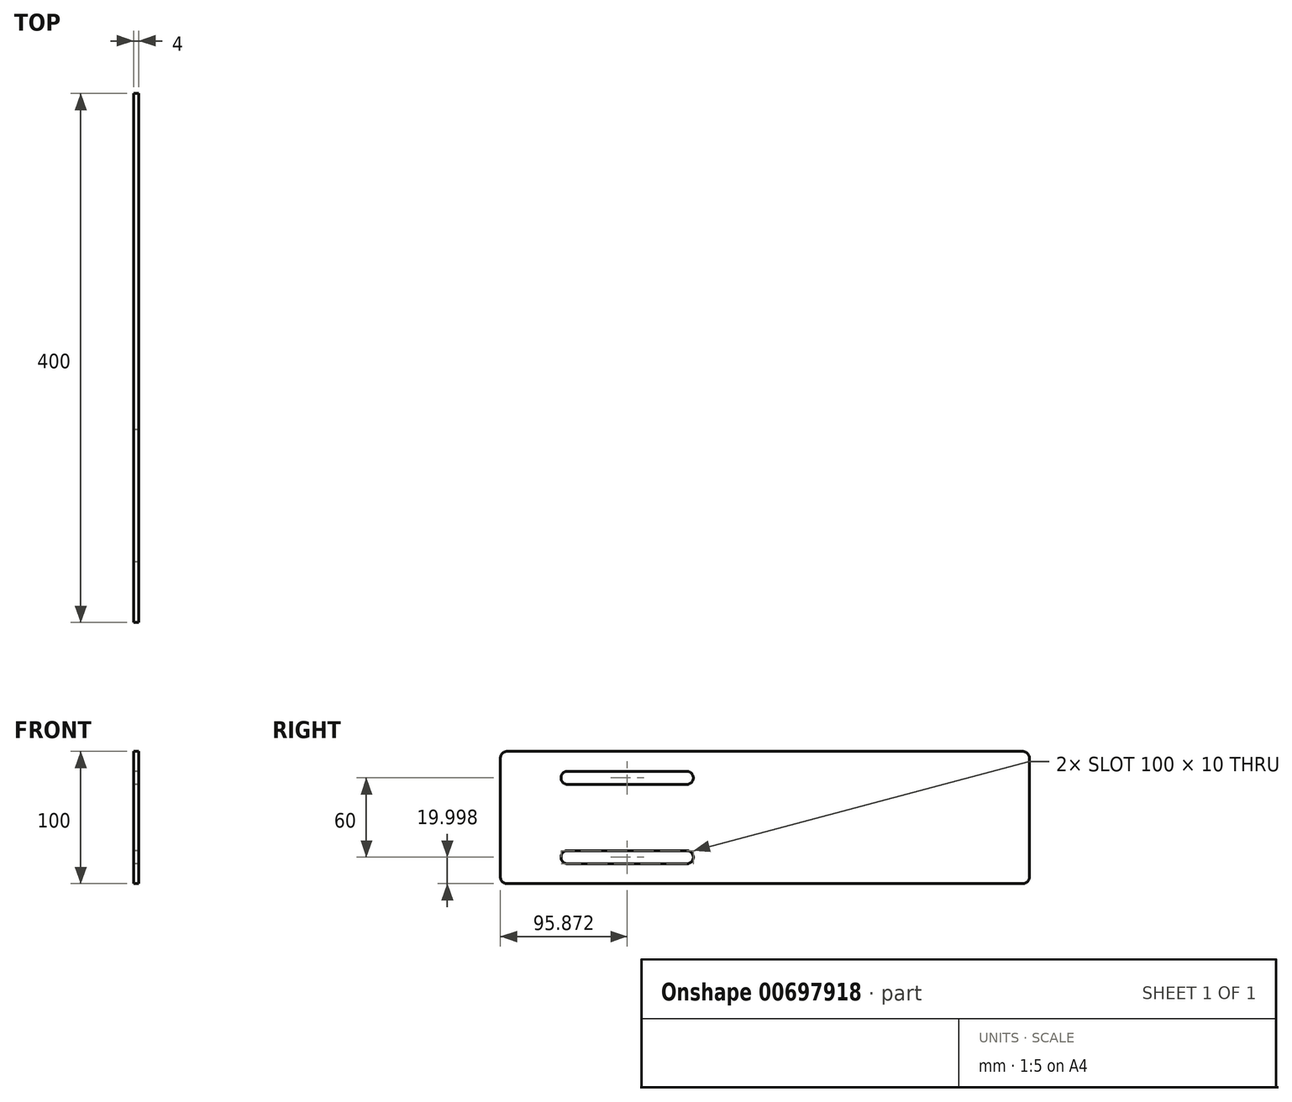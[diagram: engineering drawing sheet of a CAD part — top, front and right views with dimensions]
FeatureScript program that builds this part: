
annotation { "Feature Type Name" : "Feature", "Feature Type Description" : "" }
export const myFeature = defineFeature(function(context is Context, id is Id, definition is map)
    precondition{}
    {
        {
            var Q0;
            Q0=qCreatedBy(makeId("Right.planeOp"),FACE);
            var sketch = newSketch(context, id + "F0", { "sketchPlane" : qUnion([Q0])});
            skLineSegment(sketch, "E0.bottom", {"start": v(-184.31, 31.74) * mm, "end": v(205.69, 31.74) * mm});
            skLineSegment(sketch, "E0.top", {"start": v(-184.31, -68.26) * mm, "end": v(205.69, -68.26) * mm});
            skLineSegment(sketch, "E0.left", {"start": v(-189.31, 26.74) * mm, "end": v(-189.31, -63.26) * mm});
            skLineSegment(sketch, "E0.right", {"start": v(210.69, 26.74) * mm, "end": v(210.69, -63.26) * mm});
            skPoint(sketch, "E1.visualSharp", {"position": v(210.69, 31.74) * mm});
            skArc(sketch, "E1.filletArc", {"start": v(210.69, 26.74) * mm, "mid": v(209.22, 30.27) * mm, "end": v(205.69, 31.74) * mm});
            skPoint(sketch, "E2.visualSharp", {"position": v(210.69, -68.26) * mm});
            skArc(sketch, "E2.filletArc", {"start": v(205.69, -68.26) * mm, "mid": v(209.22, -66.8) * mm, "end": v(210.69, -63.26) * mm});
            skPoint(sketch, "E3.visualSharp", {"position": v(-189.31, -68.26) * mm});
            skArc(sketch, "E3.filletArc", {"start": v(-189.31, -63.26) * mm, "mid": v(-187.85, -66.8) * mm, "end": v(-184.31, -68.26) * mm});
            skPoint(sketch, "E4.visualSharp", {"position": v(-189.31, 31.74) * mm});
            skArc(sketch, "E4.filletArc", {"start": v(-184.31, 31.74) * mm, "mid": v(-187.85, 30.27) * mm, "end": v(-189.31, 26.74) * mm});
            skSolve(sketch);
        }
        {
            var Q0;
            Q0 = qSketchRegion(id + "F0", true);
            extrude(context, id + "F1", {"entities" : qUnion([Q0]), "depth" : 4 * mm, "offsetDistance" : 25 * mm});
        }
        {
            var Q0;
            Q0=qCreatedBy(makeId("Right.planeOp"),FACE);
            var sketch = newSketch(context, id + "F2", { "sketchPlane" : qUnion([Q0])});
            skLineSegment(sketch, "E5.bottom", {"start": v(-138.44, 16.74) * mm, "end": v(-48.44, 16.74) * mm});
            skLineSegment(sketch, "E5.top", {"start": v(-138.44, 6.74) * mm, "end": v(-48.44, 6.74) * mm});
            skLineSegment(sketch, "E5.left", {"start": v(-143.44, 11.74) * mm, "end": v(-143.44, 11.74) * mm});
            skLineSegment(sketch, "E5.right", {"start": v(-43.44, 11.74) * mm, "end": v(-43.44, 11.74) * mm});
            skPoint(sketch, "E6.firstSnap0", {"position": v(-143.44, 11.74) * mm});
            skLineSegment(sketch, "E6.bottom", {"start": v(-138.44, -43.26) * mm, "end": v(-48.44, -43.26) * mm});
            skLineSegment(sketch, "E6.top", {"start": v(-138.44, -53.26) * mm, "end": v(-48.44, -53.26) * mm});
            skLineSegment(sketch, "E6.left", {"start": v(-143.44, -48.26) * mm, "end": v(-143.44, -48.26) * mm});
            skLineSegment(sketch, "E6.right", {"start": v(-43.44, -48.26) * mm, "end": v(-43.44, -48.26) * mm});
            skPoint(sketch, "E7.visualSharp", {"position": v(-143.44, 16.74) * mm});
            skArc(sketch, "E7.filletArc", {"start": v(-138.44, 16.74) * mm, "mid": v(-141.97, 15.27) * mm, "end": v(-143.44, 11.74) * mm});
            skPoint(sketch, "E8.visualSharp", {"position": v(-143.44, 6.74) * mm});
            skArc(sketch, "E8.filletArc", {"start": v(-143.44, 11.74) * mm, "mid": v(-141.97, 8.2) * mm, "end": v(-138.44, 6.74) * mm});
            skPoint(sketch, "E9.visualSharp", {"position": v(-43.44, 6.74) * mm});
            skArc(sketch, "E9.filletArc", {"start": v(-48.44, 6.74) * mm, "mid": v(-44.9, 8.2) * mm, "end": v(-43.44, 11.74) * mm});
            skPoint(sketch, "E10.visualSharp", {"position": v(-43.44, 16.74) * mm});
            skArc(sketch, "E10.filletArc", {"start": v(-43.44, 11.74) * mm, "mid": v(-44.9, 15.27) * mm, "end": v(-48.44, 16.74) * mm});
            skPoint(sketch, "E11.visualSharp", {"position": v(-43.44, -43.26) * mm});
            skArc(sketch, "E11.filletArc", {"start": v(-43.44, -48.26) * mm, "mid": v(-44.9, -44.73) * mm, "end": v(-48.44, -43.26) * mm});
            skPoint(sketch, "E12.visualSharp", {"position": v(-43.44, -53.26) * mm});
            skArc(sketch, "E12.filletArc", {"start": v(-48.44, -53.26) * mm, "mid": v(-44.9, -51.8) * mm, "end": v(-43.44, -48.26) * mm});
            skPoint(sketch, "E13.visualSharp", {"position": v(-143.44, -43.26) * mm});
            skArc(sketch, "E13.filletArc", {"start": v(-138.44, -43.26) * mm, "mid": v(-141.97, -44.73) * mm, "end": v(-143.44, -48.26) * mm});
            skPoint(sketch, "E14.visualSharp", {"position": v(-143.44, -53.26) * mm});
            skArc(sketch, "E14.filletArc", {"start": v(-143.44, -48.26) * mm, "mid": v(-141.97, -51.8) * mm, "end": v(-138.44, -53.26) * mm});
            skSolve(sketch);
        }
        {
            var Q0;
            Q0 = qSketchRegion(id + "F2", true);
            extrude(context, id + "F3", {"entities" : qUnion([Q0]), "operationType" : NewBodyOperationType.REMOVE, "depth" : 25 * mm, "offsetDistance" : 25 * mm});
        }
    });
